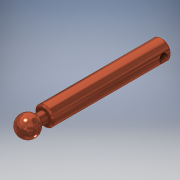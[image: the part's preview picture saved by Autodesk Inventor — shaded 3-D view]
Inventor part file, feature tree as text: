
AUTODESK INVENTOR PART (.ipt)
format: ipt  version: 2018.1 (Build 221151000, 151)  size: 136,704 bytes
history: native  units: in
note: dims shown in document units (in); Inventor stores cm internally (conversion verified against a paired STEP export)
features: sketch x3, revolve x2, chamfer x1, plane x1, hole x1
ambient origin geometry x8: Origin, YZ Plane, XZ Plane, XY Plane, X Axis, Y Axis, Z Axis, Center Point
bodies: Solid2 (feature_tree)
feature tree (8):
  revolve  "Revolution1"  [1 undecoded]
  revolve  "Revolution2"  [1 undecoded]
  chamfer  "Chamfer1"  Angle=90.0deg  [1 undecoded]
  plane  "Work Plane1"
  hole  "Hole1"  [1 undecoded]
  sketch  "Sketch1"  dims[d1=2.9119in d3=0.2185in]
  sketch  "Sketch2"  dims[d4=2.75in d6=0.1619in]
  sketch  "Sketch3"  dims[d8=0.0983in d9=90.0deg d12=0.472in d21=0.2031in d22=0.365in d23=0.2405in d24=90.0deg d25=0.038in d26=0.125in d27=45.0deg d30=0.19in d31=0.189in d32=0.75in d33=0.375in d34=0.25in d35=0.5635in d36=1.0in d37=0.8108in]
note: 4 required parameter values undecoded (feature->parameter linkage not recoverable at this tier; creation-order binding heuristic only, values carry confidence <= 0.55)